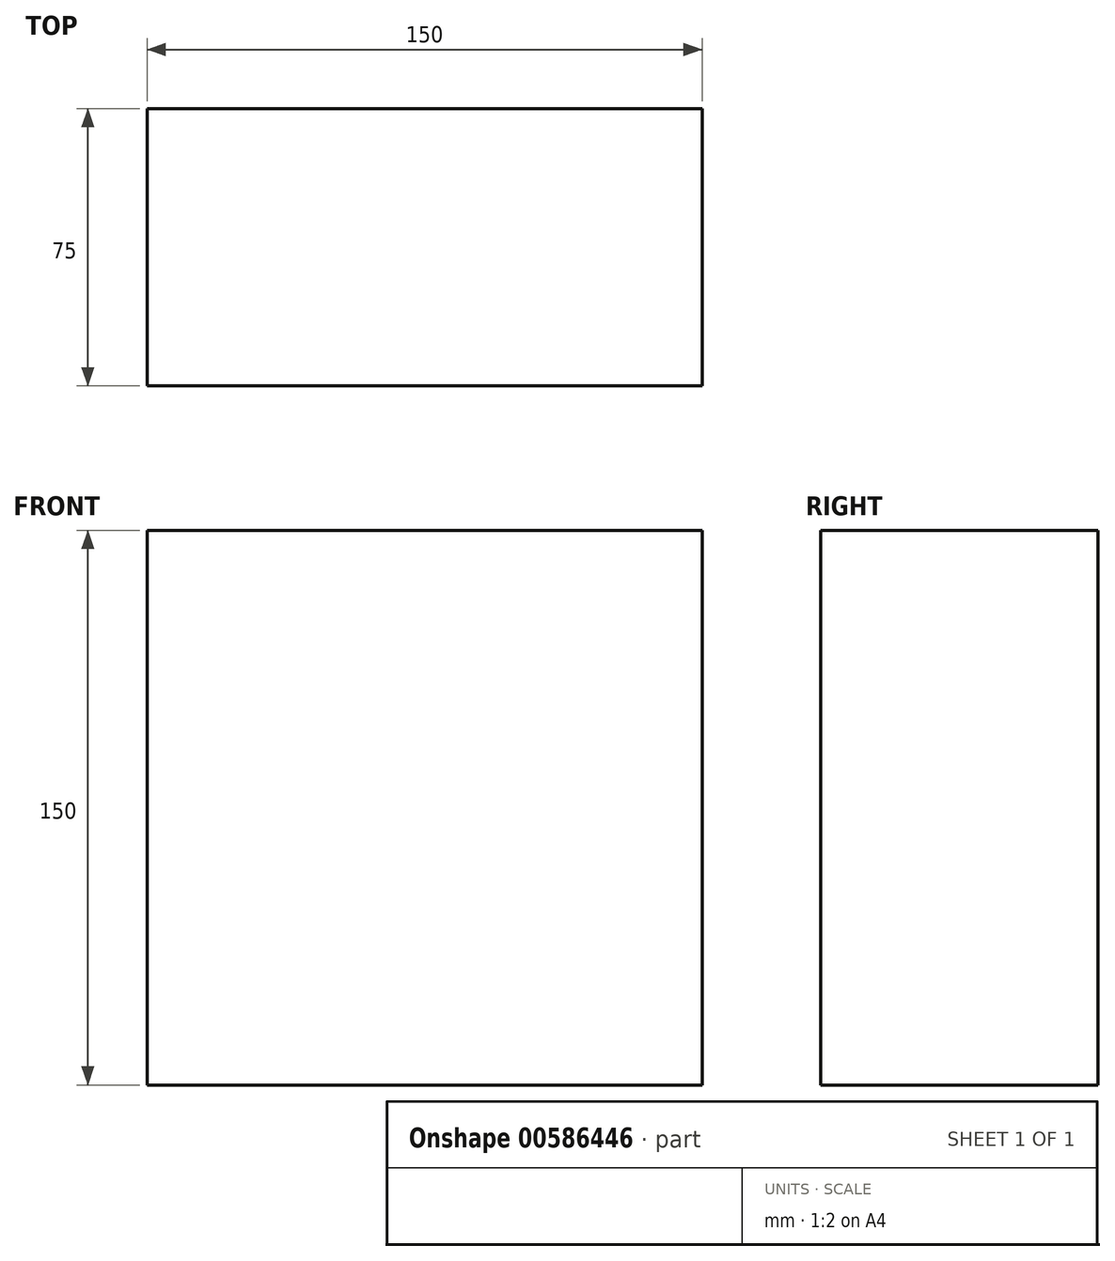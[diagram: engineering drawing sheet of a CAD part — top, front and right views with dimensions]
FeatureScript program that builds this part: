
annotation { "Feature Type Name" : "Feature", "Feature Type Description" : "" }
export const myFeature = defineFeature(function(context is Context, id is Id, definition is map)
    precondition{}
    {
        {
            var Q0;
            Q0=qCreatedBy(makeId("Top.planeOp"),FACE);
            var sketch = newSketch(context, id + "F0", { "sketchPlane" : qUnion([Q0])});
            skLineSegment(sketch, "E0.bottom", {"start": v(75, 37.5) * mm, "end": v(-75, 37.5) * mm});
            skLineSegment(sketch, "E0.top", {"start": v(75, -37.5) * mm, "end": v(-75, -37.5) * mm});
            skLineSegment(sketch, "E0.left", {"start": v(75, 37.5) * mm, "end": v(75, -37.5) * mm});
            skLineSegment(sketch, "E0.right", {"start": v(-75, 37.5) * mm, "end": v(-75, -37.5) * mm});
            skPoint(sketch, "E0.middle", {"position": v(0, 0) * mm});
            skSolve(sketch);
        }
        {
            var Q0;
            Q0 = qSketchRegion(id + "F0", true);
            extrude(context, id + "F1", {"entities" : qUnion([Q0]), "endBound" : BoundingType.SYMMETRIC, "depth" : 150 * mm, "offsetDistance" : 25.4 * mm});
        }
    });
